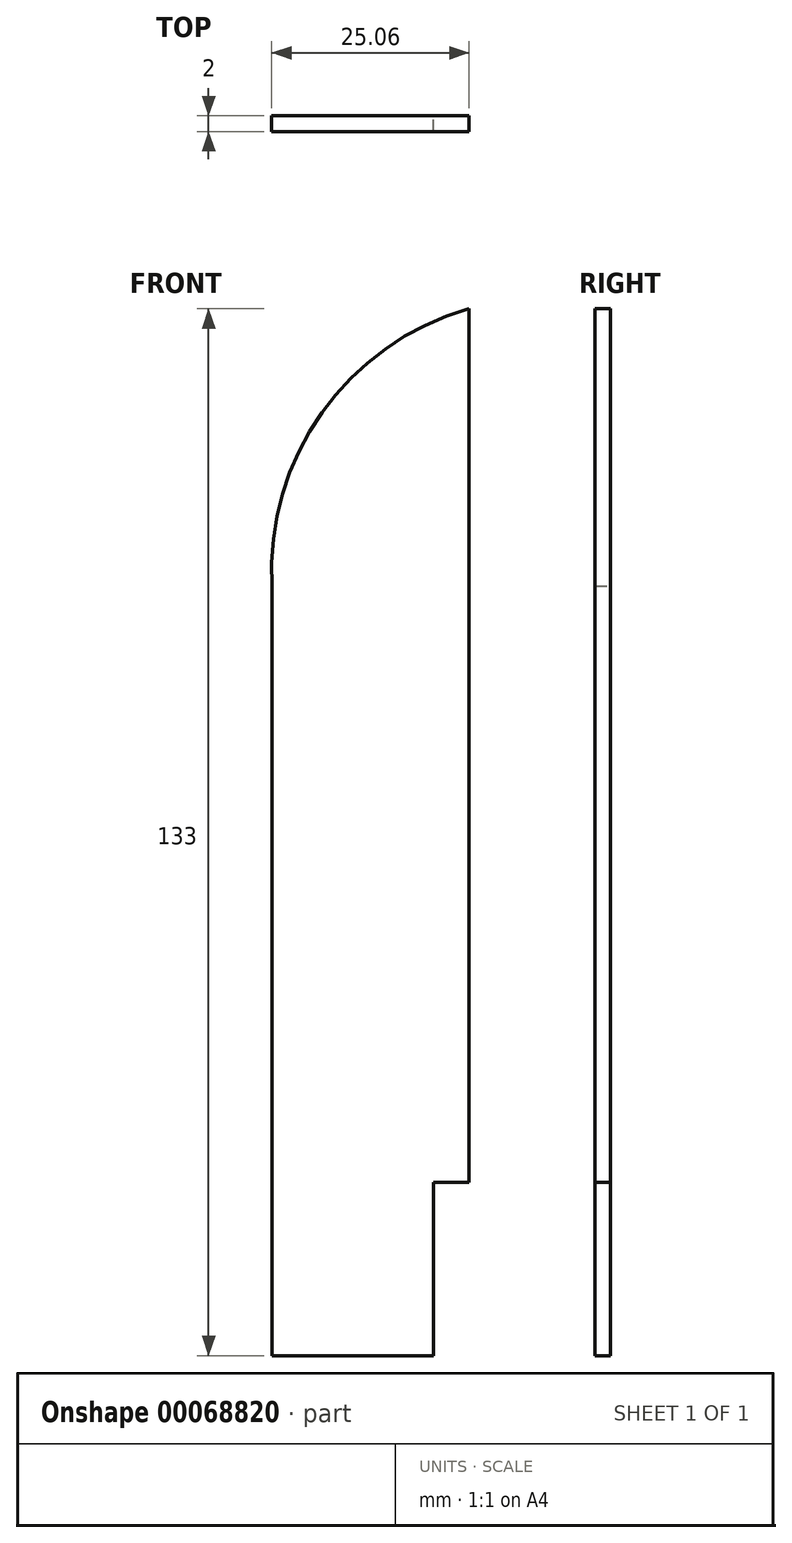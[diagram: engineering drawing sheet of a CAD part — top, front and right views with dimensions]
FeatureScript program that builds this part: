
annotation { "Feature Type Name" : "Feature", "Feature Type Description" : "" }
export const myFeature = defineFeature(function(context is Context, id is Id, definition is map)
    precondition{}
    {
        {
            var Q0;
            Q0=qCreatedBy(makeId("Front.planeOp"),FACE);
            var sketch = newSketch(context, id + "F0", { "sketchPlane" : qUnion([Q0])});
            skLineSegment(sketch, "E0", {"start": v(-247.65, -39.27) * mm, "end": v(-227.15, -39.27) * mm});
            skLineSegment(sketch, "E1", {"start": v(-227.15, -39.27) * mm, "end": v(-227.15, -17.27) * mm});
            skLineSegment(sketch, "E2", {"start": v(-227.15, -17.27) * mm, "end": v(-222.65, -17.27) * mm});
            skLineSegment(sketch, "E3", {"start": v(-222.65, -17.27) * mm, "end": v(-222.65, 93.73) * mm});
            skLineSegment(sketch, "E4", {"start": v(-247.65, 58.49) * mm, "end": v(-247.65, -39.27) * mm});
            skArc(sketch, "E5", {"start": v(-222.65, 93.73) * mm, "mid": v(-241.35, 80.5) * mm, "end": v(-247.65, 58.49) * mm});
            skSolve(sketch);
        }
        {
            var Q0;
            Q0 = qSketchRegion(id + "F0", true);
            extrude(context, id + "F1", {"entities" : qUnion([Q0]), "depth" : 2 * mm});
        }
    });
